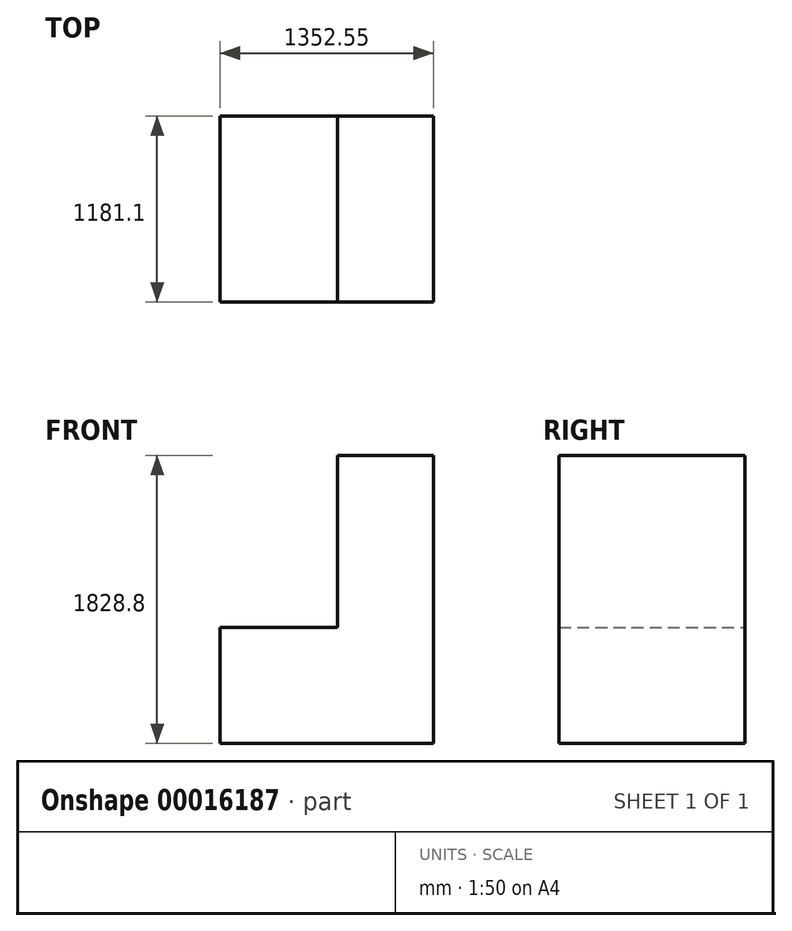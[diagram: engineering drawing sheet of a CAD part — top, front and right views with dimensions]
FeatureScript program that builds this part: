
annotation { "Feature Type Name" : "Feature", "Feature Type Description" : "" }
export const myFeature = defineFeature(function(context is Context, id is Id, definition is map)
    precondition{}
    {
        {
            var Q0;
            Q0=qCreatedBy(makeId("Top.planeOp"),FACE);
            var sketch = newSketch(context, id + "F0", { "sketchPlane" : qUnion([Q0])});
            skLineSegment(sketch, "E0.bottom", {"start": v(-327.56, -580.69) * mm, "end": v(415.39, -580.69) * mm});
            skLineSegment(sketch, "E0.top", {"start": v(-327.56, 600.41) * mm, "end": v(415.39, 600.41) * mm});
            skLineSegment(sketch, "E0.left", {"start": v(-327.56, -580.69) * mm, "end": v(-327.56, 600.41) * mm});
            skLineSegment(sketch, "E0.right", {"start": v(415.39, -580.69) * mm, "end": v(415.39, 600.41) * mm});
            skSolve(sketch);
        }
        {
            var Q0;
            Q0 = qSketchRegion(id + "F0", true);
            extrude(context, id + "F1", {"entities" : qUnion([Q0]), "depth" : 736.6 * mm});
        }
        {
            var Q0;
            Q0=qCreatedBy(makeId("Top.planeOp"),FACE);
            var sketch = newSketch(context, id + "F2", { "sketchPlane" : qUnion([Q0])});
            skLineSegment(sketch, "E1.bottom", {"start": v(415.39, 600.41) * mm, "end": v(1024.99, 600.41) * mm});
            skLineSegment(sketch, "E1.top", {"start": v(415.39, -580.69) * mm, "end": v(1024.99, -580.69) * mm});
            skLineSegment(sketch, "E1.left", {"start": v(415.39, 600.41) * mm, "end": v(415.39, -580.69) * mm});
            skLineSegment(sketch, "E1.right", {"start": v(1024.99, 600.41) * mm, "end": v(1024.99, -580.69) * mm});
            skSolve(sketch);
        }
        {
            var Q0;
            Q0 = qSketchRegion(id + "F2", true);
            extrude(context, id + "F3", {"entities" : qUnion([Q0]), "operationType" : NewBodyOperationType.ADD, "depth" : 1828.8 * mm});
        }
    });
